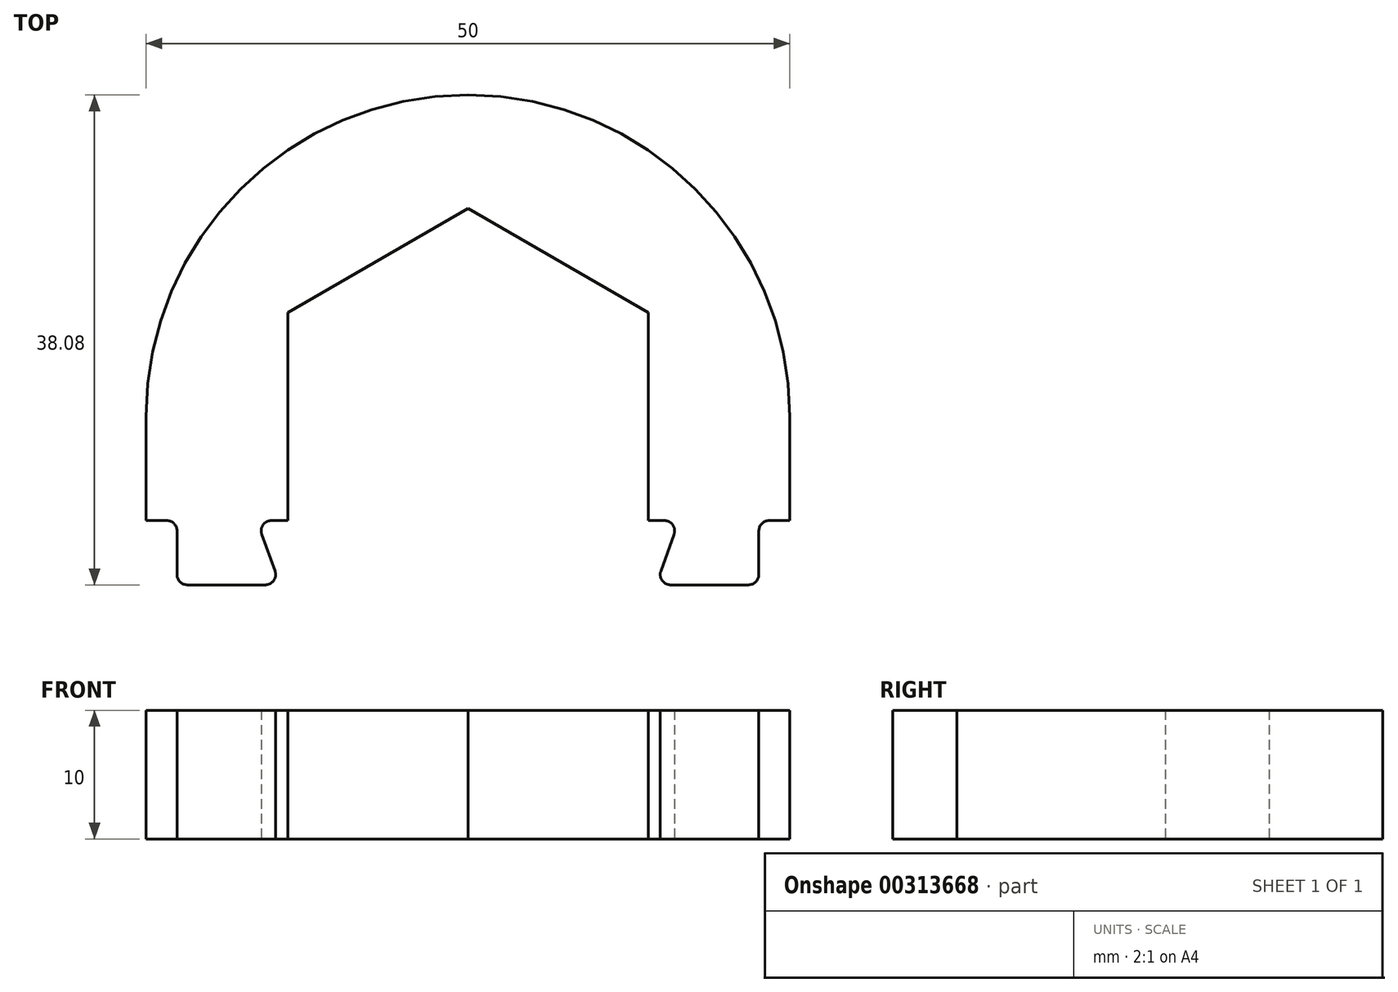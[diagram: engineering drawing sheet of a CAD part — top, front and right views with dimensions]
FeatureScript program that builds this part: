
annotation { "Feature Type Name" : "Feature", "Feature Type Description" : "" }
export const myFeature = defineFeature(function(context is Context, id is Id, definition is map)
    precondition{}
    {
        {
            var Q0;
            Q0=qCreatedBy(makeId("Top.planeOp"),FACE);
            var sketch = newSketch(context, id + "F0", { "sketchPlane" : qUnion([Q0])});
            skCircle(sketch, "E0.cCircle", {"center": v(0, 0) * mm, "radius": 14 * mm, "construction": true});
            skLineSegment(sketch, "E0.0", {"start": v(14, 8.08) * mm, "end": v(14, -8.08) * mm});
            skLineSegment(sketch, "E0.1", {"start": v(14, -8.08) * mm, "end": v(0, -16.17) * mm});
            skLineSegment(sketch, "E0.2", {"start": v(0, -16.17) * mm, "end": v(-14, -8.08) * mm});
            skLineSegment(sketch, "E0.3", {"start": v(-14, -8.08) * mm, "end": v(-14, 8.08) * mm});
            skLineSegment(sketch, "E0.4", {"start": v(-14, 8.08) * mm, "end": v(0, 16.17) * mm});
            skLineSegment(sketch, "E0.5", {"start": v(0, 16.17) * mm, "end": v(14, 8.08) * mm});
            skPoint(sketch, "E0.0.midPoint", {"position": v(14, 0) * mm});
            skArc(sketch, "E1", {"start": v(25, 0) * mm, "mid": v(0, 25) * mm, "end": v(-25, 0) * mm});
            skLineSegment(sketch, "E2.bottom", {"start": v(-25, -30) * mm, "end": v(25, -30) * mm});
            skLineSegment(sketch, "E2.left", {"start": v(-25, -30) * mm, "end": v(-25, 0) * mm});
            skLineSegment(sketch, "E2.right", {"start": v(25, -30) * mm, "end": v(25, 0) * mm});
            skLineSegment(sketch, "E3", {"start": v(-14, -8.08) * mm, "end": v(-15.26, -8.08) * mm});
            skLineSegment(sketch, "E4", {"start": v(-16.01, -9.15) * mm, "end": v(-14.99, -12.01) * mm});
            skLineSegment(sketch, "E5", {"start": v(-15.74, -13.08) * mm, "end": v(-21.8, -13.08) * mm});
            skLineSegment(sketch, "E6", {"start": v(-22.6, -12.28) * mm, "end": v(-22.6, -8.88) * mm});
            skLineSegment(sketch, "E7", {"start": v(-23.4, -8.08) * mm, "end": v(-25, -8.08) * mm});
            skPoint(sketch, "E8.visualSharp", {"position": v(-22.6, -13.08) * mm});
            skArc(sketch, "E8.filletArc", {"start": v(-22.6, -12.28) * mm, "mid": v(-22.37, -12.85) * mm, "end": v(-21.8, -13.08) * mm});
            skPoint(sketch, "E9.visualSharp", {"position": v(-14.6, -13.08) * mm});
            skArc(sketch, "E9.filletArc", {"start": v(-15.74, -13.08) * mm, "mid": v(-15.08, -12.74) * mm, "end": v(-14.99, -12.01) * mm});
            skPoint(sketch, "E10.visualSharp", {"position": v(-16.4, -8.08) * mm});
            skArc(sketch, "E10.filletArc", {"start": v(-15.26, -8.08) * mm, "mid": v(-15.92, -8.42) * mm, "end": v(-16.01, -9.15) * mm});
            skPoint(sketch, "E11.visualSharp", {"position": v(-22.6, -8.08) * mm});
            skArc(sketch, "E11.filletArc", {"start": v(-22.6, -8.88) * mm, "mid": v(-22.83, -8.32) * mm, "end": v(-23.4, -8.08) * mm});
            skLineSegment(sketch, "E12.0", {"start": v(-23.4, -7.88) * mm, "end": v(-25, -7.88) * mm});
            skArc(sketch, "E12.1", {"start": v(-22.4, -8.88) * mm, "mid": v(-22.7, -8.18) * mm, "end": v(-23.4, -7.88) * mm});
            skLineSegment(sketch, "E12.2", {"start": v(-22.4, -12.28) * mm, "end": v(-22.4, -8.88) * mm});
            skArc(sketch, "E12.3", {"start": v(-22.4, -12.28) * mm, "mid": v(-22.22, -12.7) * mm, "end": v(-21.8, -12.88) * mm});
            skLineSegment(sketch, "E12.4", {"start": v(-15.74, -12.88) * mm, "end": v(-21.8, -12.88) * mm});
            skLineSegment(sketch, "E12.5", {"start": v(-15, -7.88) * mm, "end": v(-15.26, -7.88) * mm});
            skArc(sketch, "E12.6", {"start": v(-15.26, -7.88) * mm, "mid": v(-16.08, -8.3) * mm, "end": v(-16.2, -9.22) * mm});
            skLineSegment(sketch, "E12.7", {"start": v(-16.2, -9.22) * mm, "end": v(-15.17, -12.08) * mm});
            skArc(sketch, "E12.8", {"start": v(-15.74, -12.88) * mm, "mid": v(-15.25, -12.63) * mm, "end": v(-15.17, -12.08) * mm});
            skArc(sketch, "E13.MirrorCS", {"start": v(15.74, -12.88) * mm, "mid": v(15.25, -12.63) * mm, "end": v(15.17, -12.08) * mm});
            skArc(sketch, "E14.MirrorCS", {"start": v(22.6, -12.28) * mm, "mid": v(22.37, -12.85) * mm, "end": v(21.8, -13.08) * mm});
            skArc(sketch, "E15.MirrorCS", {"start": v(22.6, -8.88) * mm, "mid": v(22.83, -8.32) * mm, "end": v(23.4, -8.08) * mm});
            skArc(sketch, "E16.MirrorCS", {"start": v(22.4, -12.28) * mm, "mid": v(22.22, -12.7) * mm, "end": v(21.8, -12.88) * mm});
            skLineSegment(sketch, "E17.MirrorCS", {"start": v(15, -7.88) * mm, "end": v(15.26, -7.88) * mm});
            skLineSegment(sketch, "E18.MirrorCS", {"start": v(14, -8.08) * mm, "end": v(15.26, -8.08) * mm});
            skLineSegment(sketch, "E19.MirrorCS", {"start": v(15.74, -13.08) * mm, "end": v(21.8, -13.08) * mm});
            skArc(sketch, "E20.MirrorCS", {"start": v(15.26, -7.88) * mm, "mid": v(16.08, -8.3) * mm, "end": v(16.2, -9.22) * mm});
            skArc(sketch, "E21.MirrorCS", {"start": v(22.4, -8.88) * mm, "mid": v(22.7, -8.18) * mm, "end": v(23.4, -7.88) * mm});
            skArc(sketch, "E22.MirrorCS", {"start": v(15.26, -8.08) * mm, "mid": v(15.92, -8.42) * mm, "end": v(16.01, -9.15) * mm});
            skPoint(sketch, "E23.MirrorP", {"position": v(16.4, -8.08) * mm});
            skArc(sketch, "E24.MirrorCS", {"start": v(15.74, -13.08) * mm, "mid": v(15.08, -12.74) * mm, "end": v(14.99, -12.01) * mm});
            skPoint(sketch, "E25.MirrorP", {"position": v(22.6, -8.08) * mm});
            skLineSegment(sketch, "E26.MirrorCS", {"start": v(15.74, -12.88) * mm, "end": v(21.8, -12.88) * mm});
            skPoint(sketch, "E27.MirrorP", {"position": v(22.6, -13.08) * mm});
            skLineSegment(sketch, "E28.MirrorCS", {"start": v(23.4, -8.08) * mm, "end": v(25, -8.08) * mm});
            skLineSegment(sketch, "E29.MirrorCS", {"start": v(23.4, -7.88) * mm, "end": v(25, -7.88) * mm});
            skLineSegment(sketch, "E30.MirrorCS", {"start": v(22.6, -12.28) * mm, "end": v(22.6, -8.88) * mm});
            skLineSegment(sketch, "E31.MirrorCS", {"start": v(16.2, -9.22) * mm, "end": v(15.17, -12.08) * mm});
            skLineSegment(sketch, "E32.MirrorCS", {"start": v(22.4, -12.28) * mm, "end": v(22.4, -8.88) * mm});
            skLineSegment(sketch, "E33.MirrorCS", {"start": v(16.01, -9.15) * mm, "end": v(14.99, -12.01) * mm});
            skSolve(sketch);
        }
        {
            var Q0;
            {var subQ5=sQuery(id+"F0.wireOp",EDGE,"E0.4");Q0=makeQuery(id+"F0.imprint","IMPRINT",FACE,{"disambiguationData":[TD([[makeQuery(id+"F0.imprint","IMPRINT",EDGE,{"derivedFrom":subQ5}),1.0]])]});}
            extrude(context, id + "F1", {"entities" : qUnion([Q0]), "depth" : 10 * mm});
        }
    });
